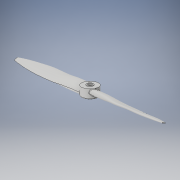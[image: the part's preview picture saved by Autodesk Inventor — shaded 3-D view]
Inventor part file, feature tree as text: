
AUTODESK INVENTOR PART (.ipt)
format: ipt  version: 2018 (Build 220112000, 112)  size: 1,662,464 bytes
history: native  units: mm
features: sketch x9, plane x7, other x3, revolve x1, loft x1, fillet x1, pattern_circular x1
ambient origin geometry x8: Origin, YZ Plane, XZ Plane, XY Plane, X Axis, Y Axis, Z Axis, Center Point
bodies: Solid1 (feature_tree)
feature tree (23):
  revolve  "Revolution1"  [1 undecoded]
  plane  "Work Plane1"
  plane  "Work Plane2"
  plane  "Work Plane3"
  plane  "Work Plane4"
  plane  "Work Plane5"
  plane  "Work Plane6"
  sketch  "Sketch2"  dims[d2=3.0mm d3=1.5mm d4=22.0mm]
  sketch  "Sketch3"  dims[d5=2.0mm]
  sketch  "Sketch4"  dims[d6=1.5mm]
  sketch  "Sketch5"  dims[d7=1.5mm]
  sketch  "Sketch6"  dims[d8=90.0deg]
  sketch  "Sketch7"  dims[d9=56.14mm d10=96.77mm d11=126.14mm d12=157.8mm d13=189.33mm d14=220.0mm d20=40.0mm]
  plane  "Work Plane7"
  sketch  "Sketch8"  dims[d24=33.278655mm]
  loft  "Loft1"
  fillet  "Fillet1"  Radius=22.0mm
  other  "Work Axis1"
  pattern_circular  "Circular Pattern1"  Count=4  [1 undecoded]
  sketch  "Sketch1"  dims[d0=5.0mm d1=20.0mm]
  other  "Image1"
  sketch  "Sketch10"  dims[d76=8.695358mm d84=13.02mm d85=15.153mm d86=15.153mm d87=13.012mm d88=9.821mm d95=13.02mm d96=15.153mm d97=15.153mm d98=13.012mm d99=9.821mm d100=221.460376mm d102=176.089529mm d131=13.02mm d132=10.0mm d135=15.153mm d136=10.0mm d142=10.0mm d143=15.153mm d150=13.012mm d151=10.0mm d152=9.821mm d153=10.0mm d154=12.0mm d155=0.0mm d156=90.0deg d157=0.0mm d158=90.0deg d159=0.0mm d160=90.0deg d161=0.0mm d162=90.0deg d163=0.0mm d164=90.0deg d165=0.0mm d166=90.0deg d167=0.0mm d168=90.0deg d169=2.0mm d170=2.0mm d171=2.0mm d172=7.436mm d173=2.0mm d174=7.969mm d175=2.0mm d176=5.859mm d177=2.0mm d178=0.313mm d179=2.0mm d180=8.125mm d181=2.0mm d182=9.277mm d183=2.0mm d184=1.18mm d185=20.0mm d186=360.0deg]
  other  "Work Axis2"
note: 2 required parameter values undecoded (feature->parameter linkage not recoverable at this tier; creation-order binding heuristic only, values carry confidence <= 0.55)